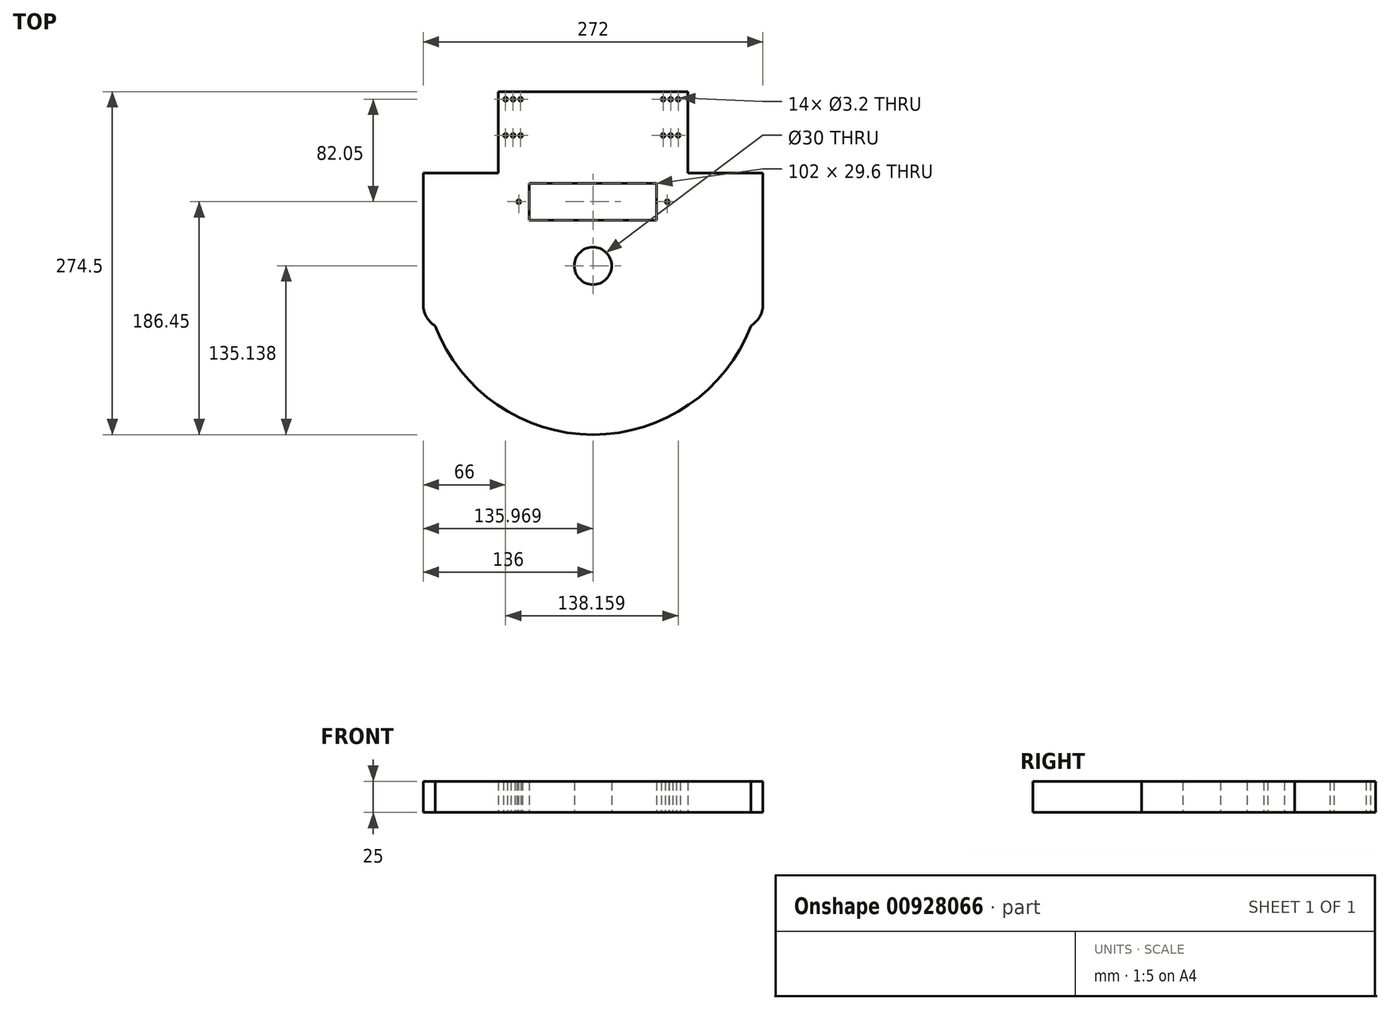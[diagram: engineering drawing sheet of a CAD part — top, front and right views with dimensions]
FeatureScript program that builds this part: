
annotation { "Feature Type Name" : "Feature", "Feature Type Description" : "" }
export const myFeature = defineFeature(function(context is Context, id is Id, definition is map)
    precondition{}
    {
        {
            var Q0;
            Q0=qCreatedBy(makeId("Top.planeOp"),FACE);
            var sketch = newSketch(context, id + "F0", { "sketchPlane" : qUnion([Q0])});
            skLineSegment(sketch, "E0", {"start": v(0, 93.35) * mm, "end": v(76, 93.35) * mm});
            skLineSegment(sketch, "E1", {"start": v(76, 93.35) * mm, "end": v(76, 28.35) * mm});
            skLineSegment(sketch, "E2", {"start": v(76, 28.35) * mm, "end": v(136, 28.35) * mm});
            skLineSegment(sketch, "E3", {"start": v(136, 28.35) * mm, "end": v(136, -76.99) * mm});
            skLineSegment(sketch, "E4", {"start": v(-136, -76.99) * mm, "end": v(-136, 28.35) * mm});
            skLineSegment(sketch, "E5", {"start": v(-136, 28.35) * mm, "end": v(-76, 28.35) * mm});
            skLineSegment(sketch, "E6", {"start": v(-76, 28.35) * mm, "end": v(-76, 93.35) * mm});
            skLineSegment(sketch, "E7", {"start": v(-76, 93.35) * mm, "end": v(0, 93.35) * mm});
            skCircle(sketch, "E8", {"center": v(-70, 87.35) * mm, "radius": 1.6 * mm});
            skCircle(sketch, "E9", {"center": v(-64, 87.35) * mm, "radius": 1.6 * mm});
            skCircle(sketch, "E10", {"center": v(-58, 87.35) * mm, "radius": 1.6 * mm});
            skCircle(sketch, "E11", {"center": v(-70, 58.35) * mm, "radius": 1.6 * mm});
            skCircle(sketch, "E12", {"center": v(-64, 58.35) * mm, "radius": 1.6 * mm});
            skCircle(sketch, "E13", {"center": v(-58, 58.35) * mm, "radius": 1.6 * mm});
            skCircle(sketch, "E14", {"center": v(68.16, 87.35) * mm, "radius": 1.6 * mm});
            skCircle(sketch, "E15", {"center": v(62.16, 87.35) * mm, "radius": 1.6 * mm});
            skCircle(sketch, "E16", {"center": v(56.16, 87.35) * mm, "radius": 1.6 * mm});
            skCircle(sketch, "E17", {"center": v(68.16, 58.35) * mm, "radius": 1.6 * mm});
            skCircle(sketch, "E18", {"center": v(62.16, 58.35) * mm, "radius": 1.6 * mm});
            skCircle(sketch, "E19", {"center": v(56.16, 58.35) * mm, "radius": 1.6 * mm});
            skArc(sketch, "E20.filletArc", {"start": v(-136, -76.99) * mm, "mid": v(-133.4, -86.85) * mm, "end": v(-126.27, -94.15) * mm});
            skArc(sketch, "E21.filletArc", {"start": v(126.27, -94.15) * mm, "mid": v(133.4, -86.85) * mm, "end": v(136, -76.99) * mm});
            skLineSegment(sketch, "E22.bottom", {"start": v(-51.03, 20.1) * mm, "end": v(50.97, 20.1) * mm});
            skLineSegment(sketch, "E22.top", {"start": v(-51.03, -9.5) * mm, "end": v(50.97, -9.5) * mm});
            skLineSegment(sketch, "E22.left", {"start": v(-51.03, 20.1) * mm, "end": v(-51.03, -9.5) * mm});
            skLineSegment(sketch, "E22.right", {"start": v(50.97, 20.1) * mm, "end": v(50.97, -9.5) * mm});
            skCircle(sketch, "E23", {"center": v(0, -46.01) * mm, "radius": 15 * mm});
            skCircle(sketch, "E24", {"center": v(59.42, 5.3) * mm, "radius": 1.6 * mm});
            skPoint(sketch, "E24.centerSnap0", {"position": v(50.97, 5.3) * mm});
            skCircle(sketch, "E25", {"center": v(-59.48, 5.3) * mm, "radius": 1.6 * mm});
            skArc(sketch, "E26", {"start": v(-126.27, -94.15) * mm, "mid": v(0, -181.15) * mm, "end": v(126.27, -94.15) * mm});
            skSolve(sketch);
        }
        {
            var Q0;
            Q0 = qSketchRegion(id + "F0", true);
            extrude(context, id + "F1", {"entities" : qUnion([Q0]), "depth" : 25 * mm, "offsetDistance" : 25 * mm});
        }
        {
            var Q0;
            Q0 = qSketchRegion(id + "F0", true);
            extrude(context, id + "F2", {"entities" : qUnion([Q0]), "operationType" : NewBodyOperationType.ADD, "depth" : 25 * mm, "offsetDistance" : 25 * mm});
        }
    });
